FCSTD DOCUMENT  (FreeCAD 1.1R20260325 (Git shallow))
Label: Unnamed
License: All rights reserved
LicenseURL: https://en.wikipedia.org/wiki/All_rights_reserved
objects: App::Point×1, Sketcher::SketchObject×1, PartDesign::Body×1
note: 3 computed .brp shape members not serialized (recipe doc carries the construction recipe); baked Part::Feature solids carry a one-line shape summary decoded from their .brp

FEATURE [App::Point] Origin001
  Role = Origin
FEATURE [Sketcher::SketchObject] Sketch
  ArcFitTolerance = 1e-06
  AttachmentSupport = -> [Origin]
  ExternalTypes = [0]
  FullyConstrained = false
  MakeInternals = false
  MapMode = 5
  _ExternalGeoVersion = 1
  sketch-geometry (4):
    g0: ArcOfCircle CenterX=0 CenterY=-12.1697 CenterZ=0 NormalX=0 NormalY=0 NormalZ=1 AngleXU=0 Radius=5.41285 StartAngle=3.33064 EndAngle=6.09414
    g1: ArcOfCircle CenterX=0 CenterY=7.46878 CenterZ=0 NormalX=0 NormalY=0 NormalZ=1 AngleXU=0 Radius=9.10336 StartAngle=6.09414 EndAngle=9.61382
    g2: LineSegment StartX=-5.31642 StartY=-13.1869 StartZ=0 EndX=-8.94117 EndY=5.75805 EndZ=0
    g3: LineSegment StartX=5.31642 StartY=-13.1869 StartZ=0 EndX=8.94117 EndY=5.75805 EndZ=0
  constraints (6):
    c: Tangent(g0,g2) = 1.5708
    c: Tangent(g0,g3) = -1.5708
    c: Tangent(g1,g2) = 1.5708
    c: Tangent(g1,g3) = -1.5708
    c: PointOnObject(g0,g-2)
    c: PointOnObject(g1,g-2)
FEATURE [PartDesign::Body] Body
  AllowCompound = true
  Group = -> [Sketch]
  Origin = -> Origin
